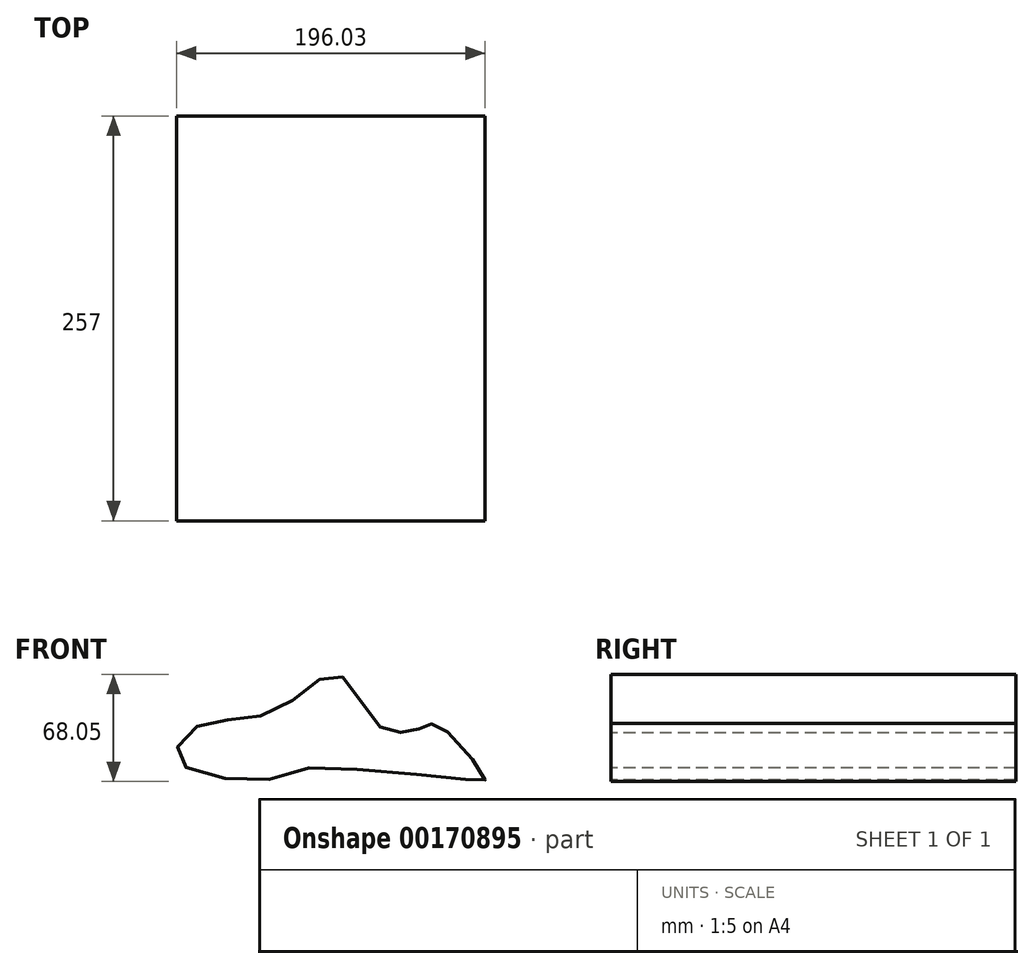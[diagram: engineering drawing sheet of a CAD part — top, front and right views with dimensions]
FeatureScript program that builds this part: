
annotation { "Feature Type Name" : "Feature", "Feature Type Description" : "" }
export const myFeature = defineFeature(function(context is Context, id is Id, definition is map)
    precondition{}
    {
        {
            var Q0;
            Q0=qCreatedBy(makeId("Front.planeOp"),FACE);
            var sketch = newSketch(context, id + "F0", { "sketchPlane" : qUnion([Q0])});
            skFitSpline(sketch, "E0", {"points": [v(-73.82, 7.66) * mm, v(-24.6, 17.39) * mm, v(15.2, 40.67) * mm, v(42.02, 7.66) * mm, v(61.77, 5) * mm, v(73.26, 8.25) * mm, v(78.86, 9.14) * mm, v(108.92, -25.05) * mm, v(101.26, -26.53) * mm, v(-10.15, -19.45) * mm, v(-18.7, -24.17) * mm, v(-84.72, -15.33) * mm, v(-73.82, 7.66) * mm]});
            skSolve(sketch);
        }
        {
            var Q0;
            Q0=sQuery(id+"F0.wireOp",EDGE,"E0");
            extrude(context, id + "F1", {"bodyType" : ToolBodyType.SURFACE, "surfaceEntities" : qUnion([Q0]), "depth" : 257 * mm});
        }
    });
